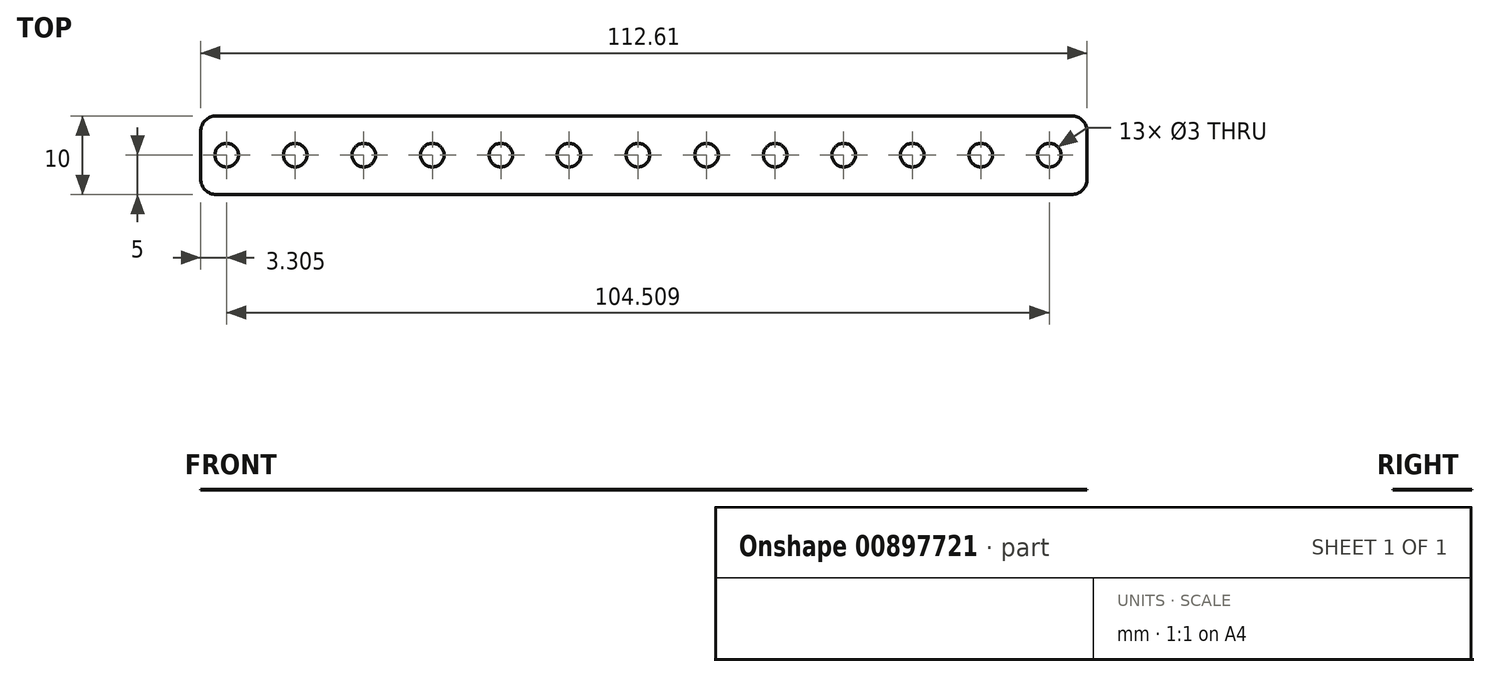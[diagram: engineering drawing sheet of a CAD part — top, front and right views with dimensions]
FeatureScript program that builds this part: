
annotation { "Feature Type Name" : "Feature", "Feature Type Description" : "" }
export const myFeature = defineFeature(function(context is Context, id is Id, definition is map)
    precondition{}
    {
        {
            var Q0;
            Q0=qCreatedBy(makeId("Top.planeOp"),FACE);
            var sketch = newSketch(context, id + "F0", { "sketchPlane" : qUnion([Q0])});
            skCircle(sketch, "E0", {"center": v(-43.55, 0) * mm, "radius": 1.5 * mm});
            skCircle(sketch, "E1.1.0.0", {"center": v(-34.84, 0) * mm, "radius": 1.5 * mm});
            skCircle(sketch, "E1.2.0.0", {"center": v(-26.13, 0) * mm, "radius": 1.5 * mm});
            skCircle(sketch, "E1.3.0.0", {"center": v(-17.42, 0) * mm, "radius": 1.5 * mm});
            skCircle(sketch, "E1.4.0.0", {"center": v(-8.7, 0) * mm, "radius": 1.5 * mm});
            skCircle(sketch, "E1.5.0.0", {"center": v(-0.06, 0) * mm, "radius": 1.5 * mm});
            skCircle(sketch, "E1.6.0.0", {"center": v(8.7, 0) * mm, "radius": 1.5 * mm});
            skCircle(sketch, "E1.7.0.0", {"center": v(17.42, 0) * mm, "radius": 1.5 * mm});
            skCircle(sketch, "E1.8.0.0", {"center": v(26.13, 0) * mm, "radius": 1.5 * mm});
            skCircle(sketch, "E1.9.0.0", {"center": v(34.84, 0) * mm, "radius": 1.5 * mm});
            skCircle(sketch, "E1.10.0.0", {"center": v(43.55, 0) * mm, "radius": 1.5 * mm});
            skCircle(sketch, "E1.11.0.0", {"center": v(52.25, 0) * mm, "radius": 1.5 * mm});
            skCircle(sketch, "E1.12.0.0", {"center": v(60.96, 0) * mm, "radius": 1.5 * mm});
            skLineSegment(sketch, "E1.direction1", {"start": v(-43.55, 0) * mm, "end": v(-34.84, 0) * mm, "construction": true});
            skLineSegment(sketch, "E2", {"start": v(-46.85, 5) * mm, "end": v(65.76, 5) * mm});
            skLineSegment(sketch, "E3", {"start": v(65.76, 5) * mm, "end": v(65.76, -5) * mm});
            skLineSegment(sketch, "E4", {"start": v(65.76, -5) * mm, "end": v(-46.85, -5) * mm});
            skLineSegment(sketch, "E5", {"start": v(-46.85, -5) * mm, "end": v(-46.85, 5) * mm});
            skLineSegment(sketch, "E6", {"start": v(-34.84, 0) * mm, "end": v(-26.13, 0) * mm, "construction": true});
            skLineSegment(sketch, "E7", {"start": v(-17.42, 0) * mm, "end": v(-26.13, 0) * mm, "construction": true});
            skLineSegment(sketch, "E8", {"start": v(-17.42, 0) * mm, "end": v(-8.7, 0) * mm, "construction": true});
            skLineSegment(sketch, "E9", {"start": v(-8.7, 0) * mm, "end": v(0, 0) * mm, "construction": true});
            skLineSegment(sketch, "E10", {"start": v(8.7, 0) * mm, "end": v(0, 0) * mm, "construction": true});
            skLineSegment(sketch, "E11", {"start": v(8.7, 0) * mm, "end": v(17.42, 0) * mm, "construction": true});
            skLineSegment(sketch, "E12", {"start": v(17.42, 0) * mm, "end": v(26.13, 0) * mm, "construction": true});
            skLineSegment(sketch, "E13", {"start": v(26.13, 0) * mm, "end": v(34.84, 0) * mm, "construction": true});
            skLineSegment(sketch, "E14", {"start": v(34.84, 0) * mm, "end": v(43.55, 0) * mm, "construction": true});
            skLineSegment(sketch, "E15", {"start": v(43.55, 0) * mm, "end": v(52.25, 0) * mm, "construction": true});
            skLineSegment(sketch, "E16", {"start": v(52.25, 0) * mm, "end": v(60.96, 0) * mm, "construction": true});
            skSolve(sketch);
        }
        {
            var Q0;
            Q0 = qSketchRegion(id + "F0", true);
            extrude(context, id + "F1", {"entities" : qUnion([Q0]), "depth" : 1 / 203.2 * mm, "offsetDistance" : 25.4 * mm});
        }
        {
            var Q0;
            Q0=makeQuery(id+"F1.opExtrude","SWEPT_EDGE",EDGE,{"disambiguationData":[OSD([sQuery(id+"F0.wireOp",EDGE,"E2"),sQuery(id+"F0.wireOp",EDGE,"E5")])]});
            var Q1;
            Q1=makeQuery(id+"F1.opExtrude","SWEPT_EDGE",EDGE,{"disambiguationData":[OSD([sQuery(id+"F0.wireOp",EDGE,"E4"),sQuery(id+"F0.wireOp",EDGE,"E5")])]});
            var Q2;
            Q2=makeQuery(id+"F1.opExtrude","SWEPT_EDGE",EDGE,{"disambiguationData":[OSD([sQuery(id+"F0.wireOp",EDGE,"E2"),sQuery(id+"F0.wireOp",EDGE,"E3")])]});
            var Q3;
            Q3=makeQuery(id+"F1.opExtrude","SWEPT_EDGE",EDGE,{"disambiguationData":[OSD([sQuery(id+"F0.wireOp",EDGE,"E3"),sQuery(id+"F0.wireOp",EDGE,"E4")])]});
            fillet(context, id + "F2", {"entities" : qUnion([Q0, Q1, Q2, Q3]), "radius" : 2 * mm, "tangentPropagation" : true, "allowEdgeOverflow" : false});
        }
    });
